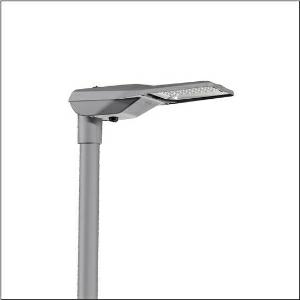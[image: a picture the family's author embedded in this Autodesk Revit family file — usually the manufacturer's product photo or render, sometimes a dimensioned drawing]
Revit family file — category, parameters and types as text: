
# Revit family: streetlight_sl_21_iq_mini___p0_8a_5xe2u31y08hb_44a6
name_source: partatom
category: Lighting Fixtures
units: mm (PartAtom-declared; Revit-internal decimal feet)

## family parameters
Cut with Voids When Loaded = No
Host = Face
Light Source = No
Part Type = Normal
Room Calculation Point = No
Round Connector Dimension = Use Diameter
Shared = No

## types (1)
- --- (1 x LED, 9830 lm, 71 W, 3000K)
    Apparent Load = 71 VA
    CIE Flux Codes = 33 69 96 100 100
    Color Rendering = 70
    Color Temperature = 3000K
    Default Elevation = 1800 mm
    Description = Streetlight SL 21 iQ mini, mast luminaire, primary light control with lens, of PMMA, primary optical cover: cover, of toughened safety glass, transparent, light distribution: P0.8a, light emission: direct distribution, primary light characteristic: asymmetric, installation type: post-top, side-entry, LED, High Power LED, rated luminous flux: 9.830lm, luminous efficacy: 139lm/W, light colour: 730, colour temperature: 3000K, control gear: iQ-Street Remote, D4i with power reduction, control: pre-setting: logarithmic dimming characteristic, Street-Remote, Auto-Match, Temp-Guard, Lumen-Switch, Night-Set, Smart-Wire, Light-Fading, Desk-Remote (wireless, voltage-free reading and setting of iQ features in the workshop via application-optimized NFC function/RFID function), optimised constant luminous flux control (CLO 2.0), mains connection: 220..240V, AC, 50/60Hz, start of lifetime: 71W, end of service life: 75W, reduction: 30W, luminaire housing, of diecast aluminium, powder-coated, SITECO metallic grey (DB 702S), corrosivity category C5 high according to DIN EN ISO 12944, please order mast flange separately, inclination adjustable: 0°, 5°, 10°, 15°, sealing non-destructively replaceable, multi-level sealing system, length: 628mm, width: 235mm, height: 110mm, mast flange for spigot size: 42mm (side-entry): 5XC10008XM4, 60/48mm (side-entry/post-top): 5XC10108XM2, 76/60mm (side-entry/post-top): 5XC10108XM1, mounting height: 4..8m, Smart Interface below and above, protection rating (complete): IP66, insulation class (complete): insulation class II (safety insulation), certification: CE, ENEC, ENEC+, VDE, impact resistance: IK10, permissible operating ambient temperature for outdoor applications: -40..+50°C, standard-compliant lighting for roads and squares, packaging unit: 1 piece

Light Distribution: P0.8a
    Height = 110 mm
    Lamp = 1 x LED
    Lamp Light Flux = 9830 lm
    Lamp Power = 71 W
    Lamp count = 1
    Length = 625 mm
    Luminous efficacy = 138 lm/W
    Manufacturer = Siteco
    ModVariant = No
    Model = 5XE2U31Y08HB
    Number of Poles = 1
    OnlyDefault = Yes
    Power Factor = 1
    Product Name = Streetlight SL 21 iQ mini | P0.8a
    Product group = mast luminaire | pylon top
    ProductGroupID = 6100
    Protection Class = Protection class II
    Protection Degree = IP 66
    RLX_Detail_Level = 1
    RLX_Emergency_Light_Flux = 0 lm
    RLX_Emergency_Type = 0
    RLX_Emergency_Type_DB = No
    RlxData = <blob elided: 92329 chars, md5=c43a6736>
    Socket = socket
    Standby Power = 0 W
    System Light Flux = 9830 lm
    System Power = 71 W
    Type Comments = factory setting: luminous flux: 100 % | dim-lin: 254 | 716 mA
    Type Image = l_1003514.jpg
    URL = http://relux.com
    VarID = @adj_081763
    Voltage = 0 V
    Weight = 0.00 kg
    Width = 234 mm

## geometry (parser evidence)
native form markers: Blend x4, Sweep x11
no freeform markers — native parametric forms only
